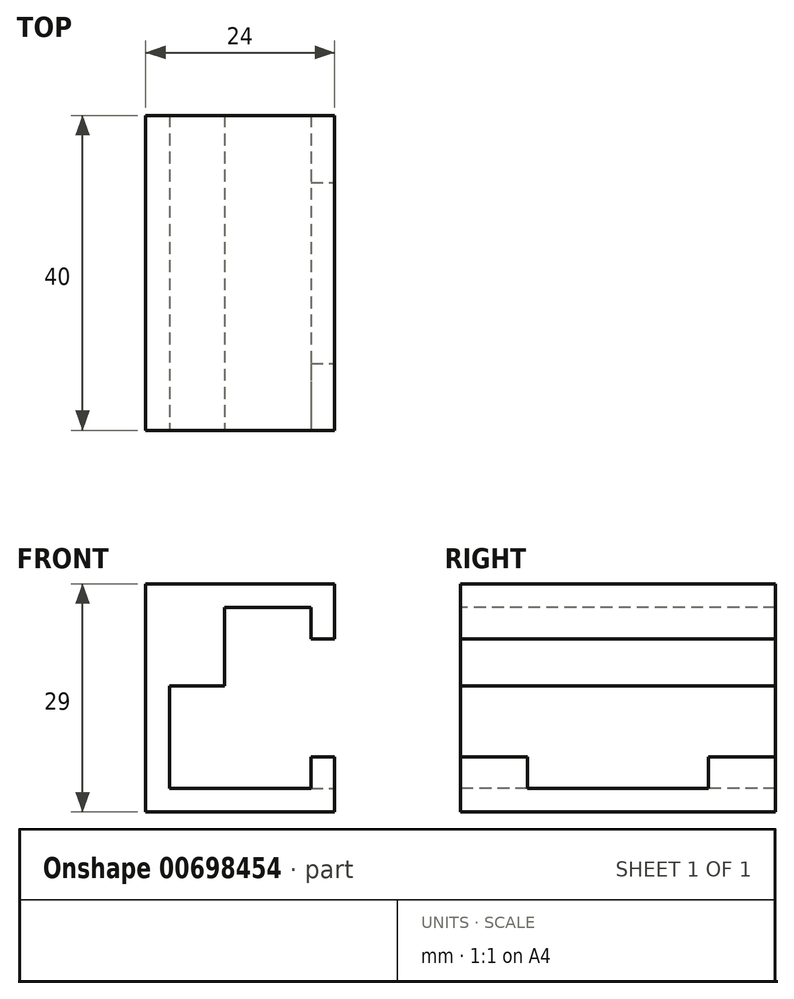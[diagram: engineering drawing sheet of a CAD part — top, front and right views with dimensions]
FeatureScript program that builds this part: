
annotation { "Feature Type Name" : "Feature", "Feature Type Description" : "" }
export const myFeature = defineFeature(function(context is Context, id is Id, definition is map)
    precondition{}
    {
        {
            var Q0;
            Q0=qCreatedBy(makeId("Top.planeOp"),FACE);
            var sketch = newSketch(context, id + "F0", { "sketchPlane" : qUnion([Q0])});
            skLineSegment(sketch, "E0.bottom", {"start": v(-12, 20) * mm, "end": v(12, 20) * mm});
            skLineSegment(sketch, "E0.top", {"start": v(-12, -20) * mm, "end": v(12, -20) * mm});
            skLineSegment(sketch, "E0.left", {"start": v(-12, 20) * mm, "end": v(-12, -20) * mm});
            skLineSegment(sketch, "E0.right", {"start": v(12, 20) * mm, "end": v(12, -20) * mm});
            skPoint(sketch, "E0.middle", {"position": v(0, 0) * mm});
            skSolve(sketch);
        }
        {
            var Q0;
            Q0=makeQuery(id+"F0.imprint","IMPRINT",FACE,{"disambiguationData":[TD([[makeQuery(id+"F0.imprint","IMPRINT",EDGE,{"derivedFrom":sQuery(id+"F0.wireOp",EDGE,"E0.bottom")}),-1.0]])]});
            extrude(context, id + "F1", {"entities" : qUnion([Q0]), "depth" : 29 * mm, "offsetDistance" : 25.4 * mm});
        }
        {
            var Q0;
            Q0=makeQuery(id+"F1.opExtrude","SWEPT_FACE",FACE,{"disambiguationData":[OSD([sQuery(id+"F0.wireOp",EDGE,"E0.top")])]});
            var sketch = newSketch(context, id + "F2", { "sketchPlane" : qUnion([Q0])});
            skLineSegment(sketch, "E1.bottom", {"start": v(-9, 26) * mm, "end": v(9, 26) * mm});
            skLineSegment(sketch, "E1.top", {"start": v(-9, 3) * mm, "end": v(9, 3) * mm});
            skLineSegment(sketch, "E1.left", {"start": v(-9, 26) * mm, "end": v(-9, 3) * mm});
            skLineSegment(sketch, "E1.right", {"start": v(9, 26) * mm, "end": v(9, 3) * mm});
            skSolve(sketch);
        }
        {
            var Q0;
            Q0=makeQuery(id+"F2.imprint","IMPRINT",FACE,{"disambiguationData":[TD([[makeQuery(id+"F2.imprint","IMPRINT",EDGE,{"derivedFrom":sQuery(id+"F2.wireOp",EDGE,"E1.bottom")}),-1.0]])]});
            extrude(context, id + "F3", {"entities" : qUnion([Q0]), "operationType" : NewBodyOperationType.REMOVE, "oppositeDirection" : true, "depth" : 61.72 * mm, "offsetDistance" : 25.4 * mm});
        }
        {
            var Q0;
            Q0=makeQuery(id+"F1.opExtrude","SWEPT_FACE",FACE,{"disambiguationData":[OSD([sQuery(id+"F0.wireOp",EDGE,"E0.top")])]});
            var sketch = newSketch(context, id + "F4", { "sketchPlane" : qUnion([Q0])});
            skLineSegment(sketch, "E2.bottom", {"start": v(9, 22) * mm, "end": v(12, 22) * mm});
            skLineSegment(sketch, "E2.top", {"start": v(9, 7) * mm, "end": v(12, 7) * mm});
            skLineSegment(sketch, "E2.left", {"start": v(9, 22) * mm, "end": v(9, 7) * mm});
            skLineSegment(sketch, "E2.right", {"start": v(12, 22) * mm, "end": v(12, 7) * mm});
            skSolve(sketch);
        }
        {
            var Q0;
            Q0=makeQuery(id+"F4.imprint","IMPRINT",FACE,{"disambiguationData":[TD([[makeQuery(id+"F4.imprint","IMPRINT",EDGE,{"derivedFrom":sQuery(id+"F4.wireOp",EDGE,"E2.bottom")}),-1.0]])]});
            extrude(context, id + "F5", {"entities" : qUnion([Q0]), "operationType" : NewBodyOperationType.REMOVE, "oppositeDirection" : true, "depth" : 55.63 * mm, "offsetDistance" : 25.4 * mm});
        }
        {
            var Q0;
            {var subQ1=sQuery(id+"F0.wireOp",EDGE,"E0.right");Q0=makeQuery(id+"F5.boolean.opBoolean","SPLIT",FACE,{"disambiguationData":[TD([makeQuery(id+"F5.opExtrude","SWEPT_FACE",FACE,{"disambiguationData":[OSD([sQuery(id+"F4.wireOp",EDGE,"E2.top")])]})])],"derivedFrom":makeQuery(id+"F1.opExtrude","SWEPT_FACE",FACE,{"disambiguationData":[OSD([subQ1])]})});}
            var sketch = newSketch(context, id + "F6", { "sketchPlane" : qUnion([Q0])});
            skLineSegment(sketch, "E3.bottom", {"start": v(-11.5, 7) * mm, "end": v(11.5, 7) * mm});
            skLineSegment(sketch, "E3.top", {"start": v(-11.5, 3) * mm, "end": v(11.5, 3) * mm});
            skLineSegment(sketch, "E3.left", {"start": v(-11.5, 7) * mm, "end": v(-11.5, 3) * mm});
            skLineSegment(sketch, "E3.right", {"start": v(11.5, 7) * mm, "end": v(11.5, 3) * mm});
            skSolve(sketch);
        }
        {
            var Q0;
            Q0=makeQuery(id+"F6.imprint","IMPRINT",FACE,{"disambiguationData":[TD([[makeQuery(id+"F6.imprint","IMPRINT",EDGE,{"derivedFrom":sQuery(id+"F6.wireOp",EDGE,"E3.bottom")}),1.0]])]});
            extrude(context, id + "F7", {"entities" : qUnion([Q0]), "operationType" : NewBodyOperationType.REMOVE, "oppositeDirection" : true, "depth" : 5.33 * mm, "offsetDistance" : 25.4 * mm});
        }
        {
            var Q0;
            Q0=makeQuery(id+"F1.opExtrude","SWEPT_FACE",FACE,{"disambiguationData":[OSD([sQuery(id+"F0.wireOp",EDGE,"E0.top")])]});
            var sketch = newSketch(context, id + "F8", { "sketchPlane" : qUnion([Q0])});
            skLineSegment(sketch, "E4.bottom", {"start": v(-9, 26) * mm, "end": v(-2, 26) * mm});
            skLineSegment(sketch, "E4.top", {"start": v(-9, 16) * mm, "end": v(-2, 16) * mm});
            skLineSegment(sketch, "E4.left", {"start": v(-9, 26) * mm, "end": v(-9, 16) * mm});
            skLineSegment(sketch, "E4.right", {"start": v(-2, 26) * mm, "end": v(-2, 16) * mm});
            skSolve(sketch);
        }
        {
            var Q0;
            Q0=makeQuery(id+"F8.imprint","IMPRINT",FACE,{"disambiguationData":[TD([[makeQuery(id+"F8.imprint","IMPRINT",EDGE,{"derivedFrom":sQuery(id+"F8.wireOp",EDGE,"E4.bottom")}),-1.0]])]});
            extrude(context, id + "F9", {"entities" : qUnion([Q0]), "operationType" : NewBodyOperationType.ADD, "oppositeDirection" : true, "depth" : 40 * mm, "offsetDistance" : 25 * mm});
        }
    });
